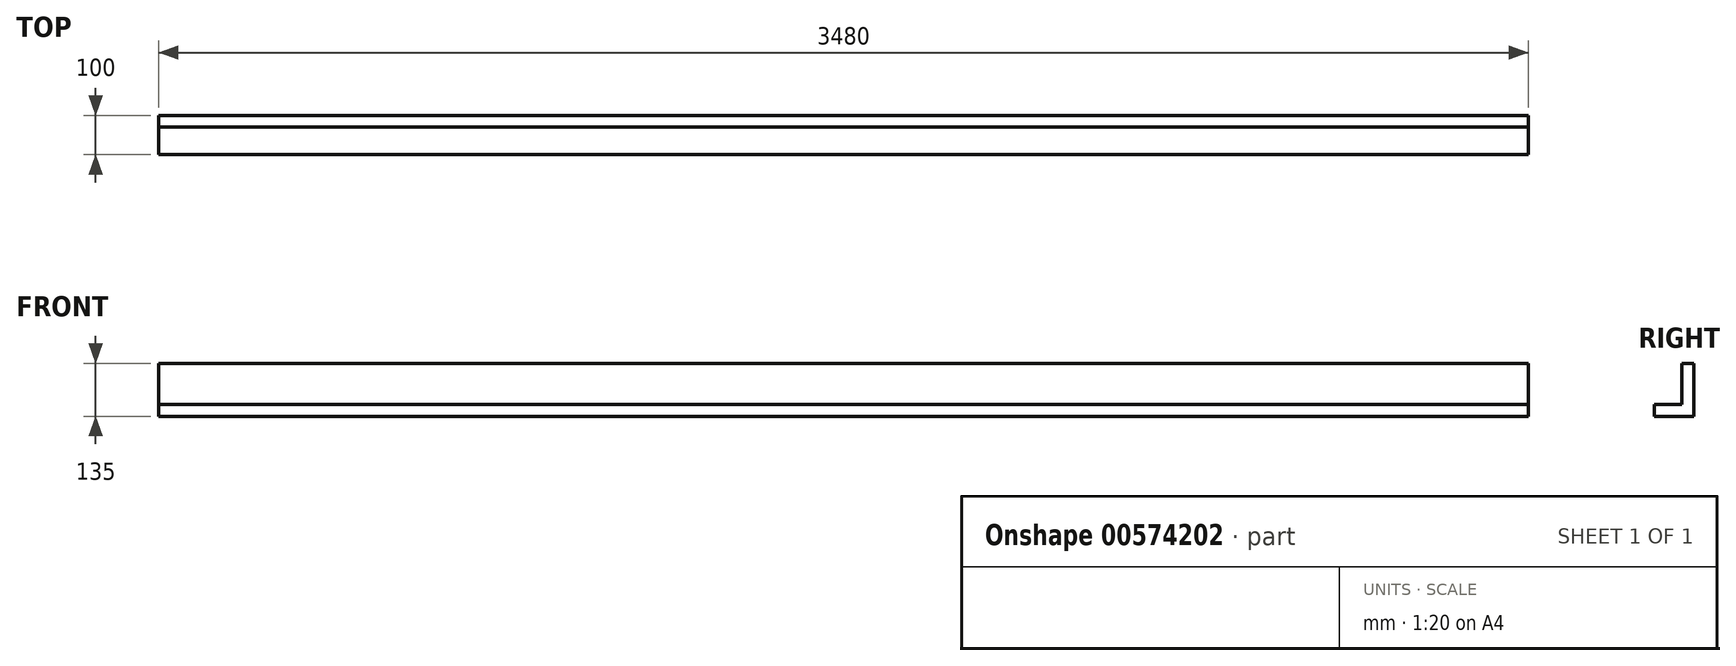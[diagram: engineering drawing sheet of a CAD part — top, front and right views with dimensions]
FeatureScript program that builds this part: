
annotation { "Feature Type Name" : "Feature", "Feature Type Description" : "" }
export const myFeature = defineFeature(function(context is Context, id is Id, definition is map)
    precondition{}
    {
        {
            var Q0;
            Q0=qCreatedBy(makeId("Right.planeOp"),FACE);
            var sketch = newSketch(context, id + "F0", { "sketchPlane" : qUnion([Q0])});
            skLineSegment(sketch, "E0", {"start": v(0, 0) * mm, "end": v(-100, 0) * mm});
            skLineSegment(sketch, "E1", {"start": v(-100, 0) * mm, "end": v(-100, 30) * mm});
            skLineSegment(sketch, "E2", {"start": v(-100, 30) * mm, "end": v(-30, 30) * mm});
            skLineSegment(sketch, "E3", {"start": v(-30, 30) * mm, "end": v(-30, 135) * mm});
            skLineSegment(sketch, "E4", {"start": v(-30, 135) * mm, "end": v(0, 135) * mm});
            skLineSegment(sketch, "E5", {"start": v(0, 135) * mm, "end": v(0, 0) * mm});
            skSolve(sketch);
        }
        {
            var Q0;
            Q0=makeQuery(id+"F0.imprint","IMPRINT",FACE,{"disambiguationData":[TD([[makeQuery(id+"F0.imprint","IMPRINT",EDGE,{"derivedFrom":sQuery(id+"F0.wireOp",EDGE,"E0")}),-1.0]])]});
            extrude(context, id + "F1", {"entities" : qUnion([Q0]), "depth" : 3480 * mm, "offsetDistance" : 25 * mm});
        }
    });
